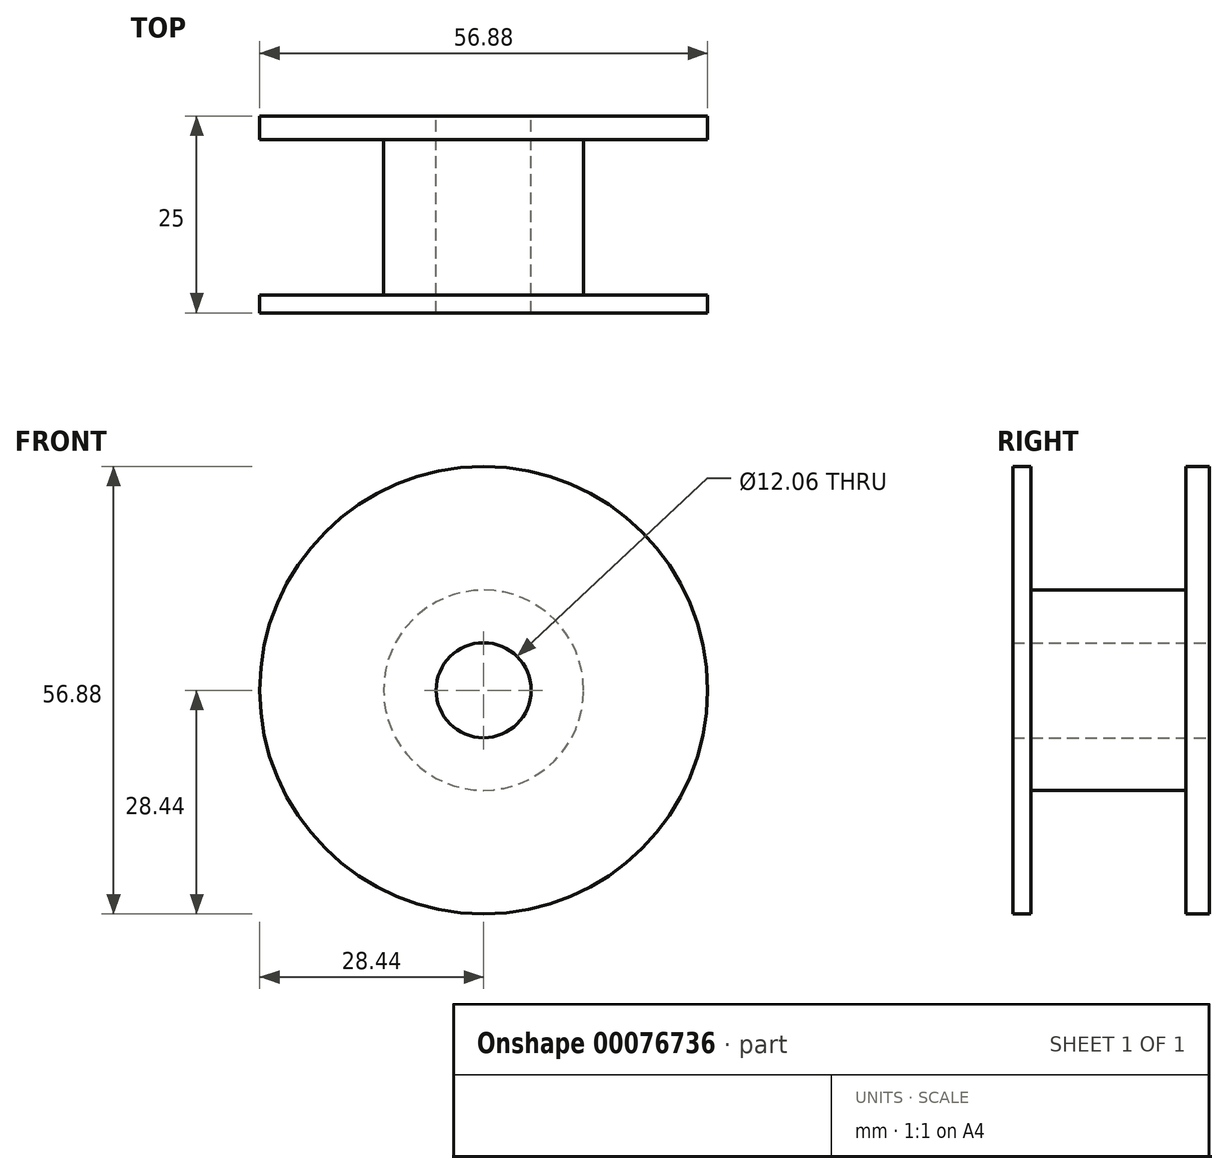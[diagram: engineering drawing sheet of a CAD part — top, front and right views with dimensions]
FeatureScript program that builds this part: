
annotation { "Feature Type Name" : "Feature", "Feature Type Description" : "" }
export const myFeature = defineFeature(function(context is Context, id is Id, definition is map)
    precondition{}
    {
        {
            var Q0;
            Q0=qCreatedBy(makeId("Front.planeOp"),FACE);
            var sketch = newSketch(context, id + "F0", { "sketchPlane" : qUnion([Q0])});
            skCircle(sketch, "E0", {"center": v(0, 0) * mm, "radius": 28.44 * mm});
            skCircle(sketch, "E1", {"center": v(0, 0) * mm, "radius": 6.03 * mm});
            skSolve(sketch);
        }
        {
            var Q0;
            Q0=qCreatedBy(makeId("Top.planeOp"),FACE);
            var sketch = newSketch(context, id + "F1", { "sketchPlane" : qUnion([Q0])});
            skLineSegment(sketch, "E2", {"start": v(-28.43, -22.72) * mm, "end": v(-12.71, -22.72) * mm});
            skLineSegment(sketch, "E3", {"start": v(-12.71, -22.72) * mm, "end": v(-12.71, -3.01) * mm});
            skLineSegment(sketch, "E4", {"start": v(-28.43, -22.72) * mm, "end": v(-28.43, -3.01) * mm});
            skLineSegment(sketch, "E5", {"start": v(-28.43, -3.01) * mm, "end": v(-12.71, -3.01) * mm});
            skSolve(sketch);
        }
        {
            var Q0;
            Q0 = qSketchRegion(id + "F0", true);
            extrude(context, id + "F2", {"entities" : qUnion([Q0]), "depth" : 25 * mm});
        }
        {
            var Q0;
            Q0 = qSketchRegion(id + "F1", true);
            var Q1;
            Q1=sQuery(id+"F0.wireOp",EDGE,"E1");
            revolve(context, id + "F3", {"operationType" : NewBodyOperationType.REMOVE, "entities" : qUnion([Q0]), "axis" : qUnion([Q1]), "revolveType" : RevolveType.FULL, "oppositeDirection" : true});
        }
    });
